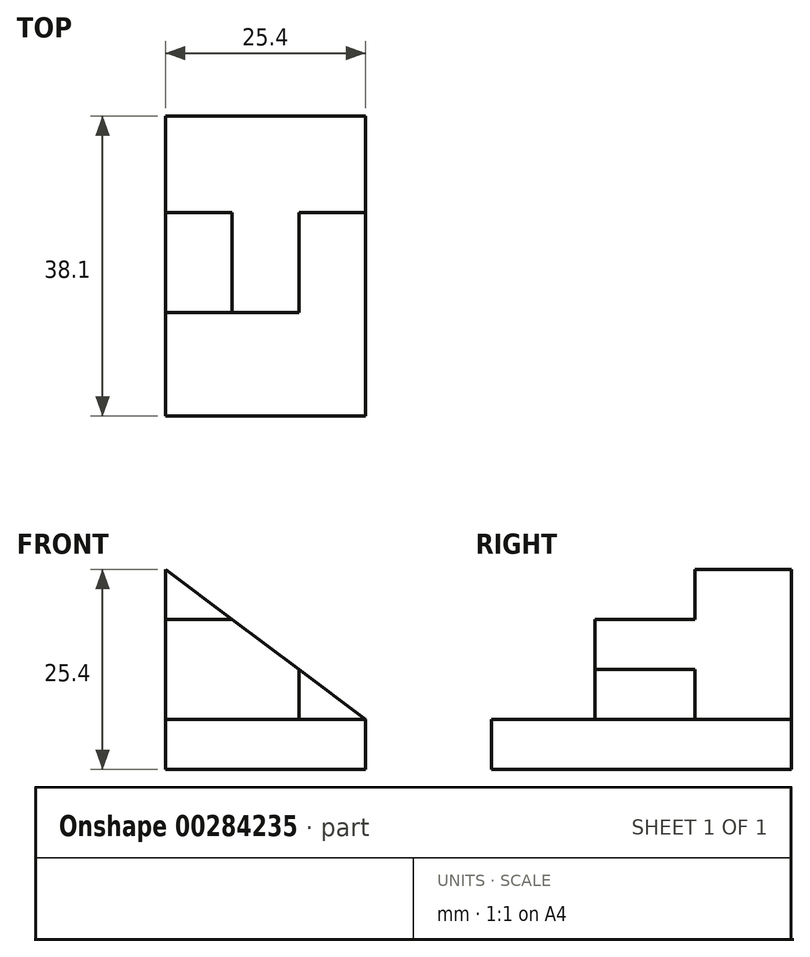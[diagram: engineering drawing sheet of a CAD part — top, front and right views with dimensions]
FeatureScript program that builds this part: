
annotation { "Feature Type Name" : "Feature", "Feature Type Description" : "" }
export const myFeature = defineFeature(function(context is Context, id is Id, definition is map)
    precondition{}
    {
        {
            var Q0;
            Q0=qCreatedBy(makeId("Front.planeOp"),FACE);
            var sketch = newSketch(context, id + "F0", { "sketchPlane" : qUnion([Q0])});
            skLineSegment(sketch, "E0.bottom", {"start": v(0, 0) * mm, "end": v(25.4, 0) * mm});
            skLineSegment(sketch, "E0.top", {"start": v(0, 6.35) * mm, "end": v(25.4, 6.35) * mm});
            skLineSegment(sketch, "E0.left", {"start": v(0, 0) * mm, "end": v(0, 6.35) * mm});
            skLineSegment(sketch, "E0.right", {"start": v(25.4, 0) * mm, "end": v(25.4, 6.35) * mm});
            skSolve(sketch);
        }
        {
            var Q0;
            Q0 = qSketchRegion(id + "F0", true);
            extrude(context, id + "F1", {"entities" : qUnion([Q0]), "endBound" : BoundingType.SYMMETRIC, "depth" : 38.1 * mm});
        }
        {
            var Q0;
            Q0=makeQuery(id+"F1.opExtrude","SWEPT_FACE",FACE,{"disambiguationData":[OSD([sQuery(id+"F0.wireOp",EDGE,"E0.top")])]});
            var sketch = newSketch(context, id + "F2", { "sketchPlane" : qUnion([Q0])});
            skLineSegment(sketch, "E1", {"start": v(0, 19.05) * mm, "end": v(0, -5.88) * mm});
            skLineSegment(sketch, "E2", {"start": v(0, -5.88) * mm, "end": v(25.4, -5.88) * mm});
            skLineSegment(sketch, "E3", {"start": v(25.4, -5.88) * mm, "end": v(25.4, 19.05) * mm});
            skLineSegment(sketch, "E4", {"start": v(25.4, 19.05) * mm, "end": v(0, 19.05) * mm});
            skSolve(sketch);
        }
        {
            var Q0;
            Q0=makeQuery(id+"F2.imprint","IMPRINT",FACE,{"disambiguationData":[TD([[makeQuery(id+"F2.imprint","IMPRINT",EDGE,{"derivedFrom":sQuery(id+"F2.wireOp",EDGE,"E1")}),-1.0]])]});
            extrude(context, id + "F3", {"entities" : qUnion([Q0]), "operationType" : NewBodyOperationType.ADD, "depth" : 19.05 * mm});
        }
        {
            var Q0;
            Q0=makeQuery(id+"F3.boolean.opBoolean","MERGE",FACE,{"derivedFrom":[makeQuery(id+"F1.opExtrude","SWEPT_FACE",FACE,{"disambiguationData":[OSD([sQuery(id+"F0.wireOp",EDGE,"E0.right")])]}),makeQuery(id+"F3.opExtrude","SWEPT_FACE",FACE,{"disambiguationData":[OSD([sQuery(id+"F2.wireOp",EDGE,"E3")])]})]});
            var sketch = newSketch(context, id + "F4", { "sketchPlane" : qUnion([Q0])});
            skLineSegment(sketch, "E5", {"start": v(-5.88, 6.35) * mm, "end": v(6.82, 6.35) * mm});
            skLineSegment(sketch, "E6", {"start": v(6.82, 6.35) * mm, "end": v(6.82, 12.7) * mm});
            skLineSegment(sketch, "E7", {"start": v(6.82, 12.7) * mm, "end": v(-5.88, 12.7) * mm});
            skLineSegment(sketch, "E8", {"start": v(-5.88, 12.7) * mm, "end": v(-5.88, 6.35) * mm});
            skLineSegment(sketch, "E9", {"start": v(-5.88, 19.05) * mm, "end": v(6.82, 19.05) * mm});
            skLineSegment(sketch, "E10", {"start": v(6.82, 19.05) * mm, "end": v(6.82, 25.4) * mm});
            skLineSegment(sketch, "E11", {"start": v(6.82, 25.4) * mm, "end": v(-5.88, 25.4) * mm});
            skLineSegment(sketch, "E12", {"start": v(-5.88, 25.4) * mm, "end": v(-5.88, 19.05) * mm});
            skSolve(sketch);
        }
        {
            var Q0;
            Q0=makeQuery(id+"F4.imprint","IMPRINT",FACE,{"disambiguationData":[TD([[makeQuery(id+"F4.imprint","IMPRINT",EDGE,{"derivedFrom":sQuery(id+"F4.wireOp",EDGE,"E9")}),1.0]])]});
            var Q1;
            Q1=makeQuery(id+"F4.imprint","IMPRINT",FACE,{"disambiguationData":[TD([[makeQuery(id+"F4.imprint","IMPRINT",EDGE,{"derivedFrom":sQuery(id+"F4.wireOp",EDGE,"E5")}),1.0]])]});
            extrude(context, id + "F5", {"entities" : qUnion([Q0, Q1]), "operationType" : NewBodyOperationType.REMOVE, "endBound" : BoundingType.THROUGH_ALL, "oppositeDirection" : true, "depth" : 25.4 * mm});
        }
        {
            var Q0;
            Q0=makeQuery(id+"F3.boolean.opBoolean","MERGE",FACE,{"derivedFrom":[makeQuery(id+"F1.opExtrude","CAP_FACE",FACE,{"disambiguationData":[OSD([sQuery(id+"F0.wireOp",EDGE,"E0.bottom"),sQuery(id+"F0.wireOp",EDGE,"E0.top"),sQuery(id+"F0.wireOp",EDGE,"E0.left"),sQuery(id+"F0.wireOp",EDGE,"E0.right")])],"isStart":true}),makeQuery(id+"F3.opExtrude","SWEPT_FACE",FACE,{"disambiguationData":[OSD([sQuery(id+"F2.wireOp",EDGE,"E4")])]})]});
            var sketch = newSketch(context, id + "F6", { "sketchPlane" : qUnion([Q0])});
            skLineSegment(sketch, "E13", {"start": v(-25.4, 25.4) * mm, "end": v(0, 25.4) * mm});
            skLineSegment(sketch, "E14", {"start": v(0, 25.4) * mm, "end": v(-25.4, 6.35) * mm});
            skLineSegment(sketch, "E15", {"start": v(-25.4, 6.35) * mm, "end": v(-25.4, 25.4) * mm});
            skSolve(sketch);
        }
        {
            var Q0;
            Q0=makeQuery(id+"F6.imprint","IMPRINT",FACE,{"disambiguationData":[TD([[makeQuery(id+"F6.imprint","IMPRINT",EDGE,{"derivedFrom":sQuery(id+"F6.wireOp",EDGE,"E13")}),1.0]])]});
            extrude(context, id + "F7", {"entities" : qUnion([Q0]), "operationType" : NewBodyOperationType.REMOVE, "endBound" : BoundingType.THROUGH_ALL, "oppositeDirection" : true, "depth" : 25.4 * mm});
        }
        {
            var Q0;
            Q0=makeQuery(id+"F5.boolean.opBoolean","COPY",FACE,{"derivedFrom":makeQuery(id+"F5.opExtrude","SWEPT_FACE",FACE,{"disambiguationData":[OSD([sQuery(id+"F4.wireOp",EDGE,"E6")])]})});
            var sketch = newSketch(context, id + "F8", { "sketchPlane" : qUnion([Q0])});
            skLineSegment(sketch, "E16", {"start": v(16.93, 12.7) * mm, "end": v(16.93, 6.35) * mm});
            skLineSegment(sketch, "E17", {"start": v(16.93, 6.35) * mm, "end": v(0, 6.35) * mm});
            skLineSegment(sketch, "E18", {"start": v(0, 6.35) * mm, "end": v(0, 12.7) * mm});
            skLineSegment(sketch, "E19", {"start": v(0, 12.7) * mm, "end": v(16.93, 12.7) * mm});
            skSolve(sketch);
        }
        {
            var Q0;
            Q0 = qSketchRegion(id + "F8", true);
            extrude(context, id + "F9", {"entities" : qUnion([Q0]), "operationType" : NewBodyOperationType.ADD, "depth" : 12.7 * mm});
        }
    });
